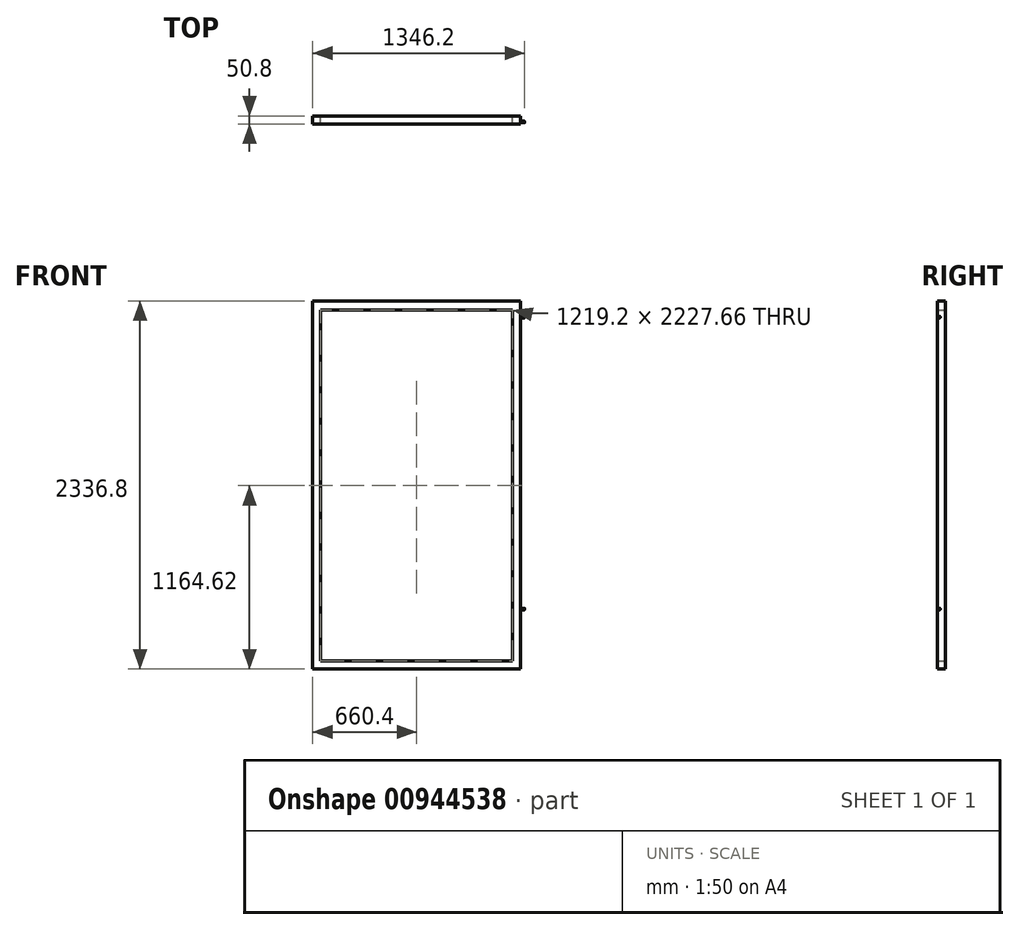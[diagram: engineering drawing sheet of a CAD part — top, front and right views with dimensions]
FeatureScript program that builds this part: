
annotation { "Feature Type Name" : "Feature", "Feature Type Description" : "" }
export const myFeature = defineFeature(function(context is Context, id is Id, definition is map)
    precondition{}
    {
        {
            var Q0;
            Q0=qCreatedBy(makeId("Front.planeOp"),FACE);
            var sketch = newSketch(context, id + "F0", { "sketchPlane" : qUnion([Q0])});
            skLineSegment(sketch, "E0.bottom", {"start": v(-114.47, 2233.26) * mm, "end": v(-63.67, 2233.26) * mm});
            skLineSegment(sketch, "E0.top", {"start": v(-114.47, -103.54) * mm, "end": v(-63.67, -103.54) * mm});
            skLineSegment(sketch, "E0.left", {"start": v(-114.47, 2233.26) * mm, "end": v(-114.47, -103.54) * mm});
            skLineSegment(sketch, "E0.right", {"start": v(-63.67, 2233.26) * mm, "end": v(-63.67, -103.54) * mm});
            skLineSegment(sketch, "E1.bottom", {"start": v(-63.67, -103.54) * mm, "end": v(1155.53, -103.54) * mm});
            skLineSegment(sketch, "E1.top", {"start": v(-63.67, -52.74) * mm, "end": v(1155.53, -52.74) * mm});
            skLineSegment(sketch, "E1.left", {"start": v(-63.67, -103.54) * mm, "end": v(-63.67, -52.74) * mm});
            skLineSegment(sketch, "E1.right", {"start": v(1155.53, -103.54) * mm, "end": v(1155.53, -52.74) * mm});
            skLineSegment(sketch, "E2.bottom", {"start": v(1155.53, -103.54) * mm, "end": v(1206.33, -103.54) * mm});
            skLineSegment(sketch, "E2.top", {"start": v(1155.53, 2233.26) * mm, "end": v(1206.33, 2233.26) * mm});
            skLineSegment(sketch, "E2.left", {"start": v(1155.53, -103.54) * mm, "end": v(1155.53, 2233.26) * mm});
            skLineSegment(sketch, "E2.right", {"start": v(1206.33, -103.54) * mm, "end": v(1206.33, 2233.26) * mm});
            skLineSegment(sketch, "E3.bottom", {"start": v(-63.67, 2233.26) * mm, "end": v(1155.53, 2233.26) * mm});
            skLineSegment(sketch, "E3.top", {"start": v(-63.67, 2174.91) * mm, "end": v(1155.53, 2174.91) * mm});
            skLineSegment(sketch, "E3.left", {"start": v(-63.67, 2233.26) * mm, "end": v(-63.67, 2174.91) * mm});
            skLineSegment(sketch, "E3.right", {"start": v(1155.53, 2233.26) * mm, "end": v(1155.53, 2174.91) * mm});
            skSolve(sketch);
        }
        {
            var Q0;
            {var subQ3=sQuery(id+"F0.wireOp",EDGE,"E2.bottom");Q0=makeQuery(id+"F0.imprint","IMPRINT",FACE,{"disambiguationData":[TD([[makeQuery(id+"F0.imprint","IMPRINT",EDGE,{"derivedFrom":subQ3}),1.0]])]});}
            var Q1;
            Q1=makeQuery(id+"F0.imprint","IMPRINT",FACE,{"disambiguationData":[TD([[makeQuery(id+"F0.imprint","IMPRINT",EDGE,{"derivedFrom":sQuery(id+"F0.wireOp",EDGE,"E3.bottom")}),-1.0]])]});
            var Q2;
            Q2=makeQuery(id+"F0.imprint","IMPRINT",FACE,{"disambiguationData":[TD([[makeQuery(id+"F0.imprint","IMPRINT",EDGE,{"derivedFrom":sQuery(id+"F0.wireOp",EDGE,"E0.bottom")}),-1.0]])]});
            var Q3;
            {var subQ0=sQuery(id+"F0.wireOp",EDGE,"E1.bottom");Q3=makeQuery(id+"F0.imprint","IMPRINT",FACE,{"disambiguationData":[TD([[makeQuery(id+"F0.imprint","IMPRINT",EDGE,{"derivedFrom":subQ0}),1.0]])]});}
            extrude(context, id + "F1", {"entities" : qUnion([Q0, Q1, Q2, Q3]), "depth" : 50.8 * mm, "offsetDistance" : 25.4 * mm});
        }
        {
            var Q0;
            Q0=makeQuery(id+"F1.opExtrude","SWEPT_FACE",FACE,{"disambiguationData":[OSD([sQuery(id+"F0.wireOp",EDGE,"E2.right")])]});
            var sketch = newSketch(context, id + "F2", { "sketchPlane" : qUnion([Q0])});
            skCircle(sketch, "E4", {"center": v(-38.1, 277.46) * mm, "radius": 4.76 * mm});
            skCircle(sketch, "E5", {"center": v(-38.1, 2131.66) * mm, "radius": 4.76 * mm});
            skSolve(sketch);
        }
        {
            var Q0;
            Q0=makeQuery(id+"F2.imprint","IMPRINT",FACE,{"disambiguationData":[TD([[makeQuery(id+"F2.imprint","IMPRINT",EDGE,{"derivedFrom":sQuery(id+"F2.wireOp",EDGE,"E5")}),1.0]])]});
            var Q1;
            Q1=makeQuery(id+"F2.imprint","IMPRINT",FACE,{"disambiguationData":[TD([[makeQuery(id+"F2.imprint","IMPRINT",EDGE,{"derivedFrom":sQuery(id+"F2.wireOp",EDGE,"E4")}),1.0]])]});
            extrude(context, id + "F3", {"entities" : qUnion([Q0, Q1]), "operationType" : NewBodyOperationType.ADD, "oppositeDirection" : true, "depth" : -25.4 * mm, "offsetDistance" : 25.4 * mm});
        }
    });
